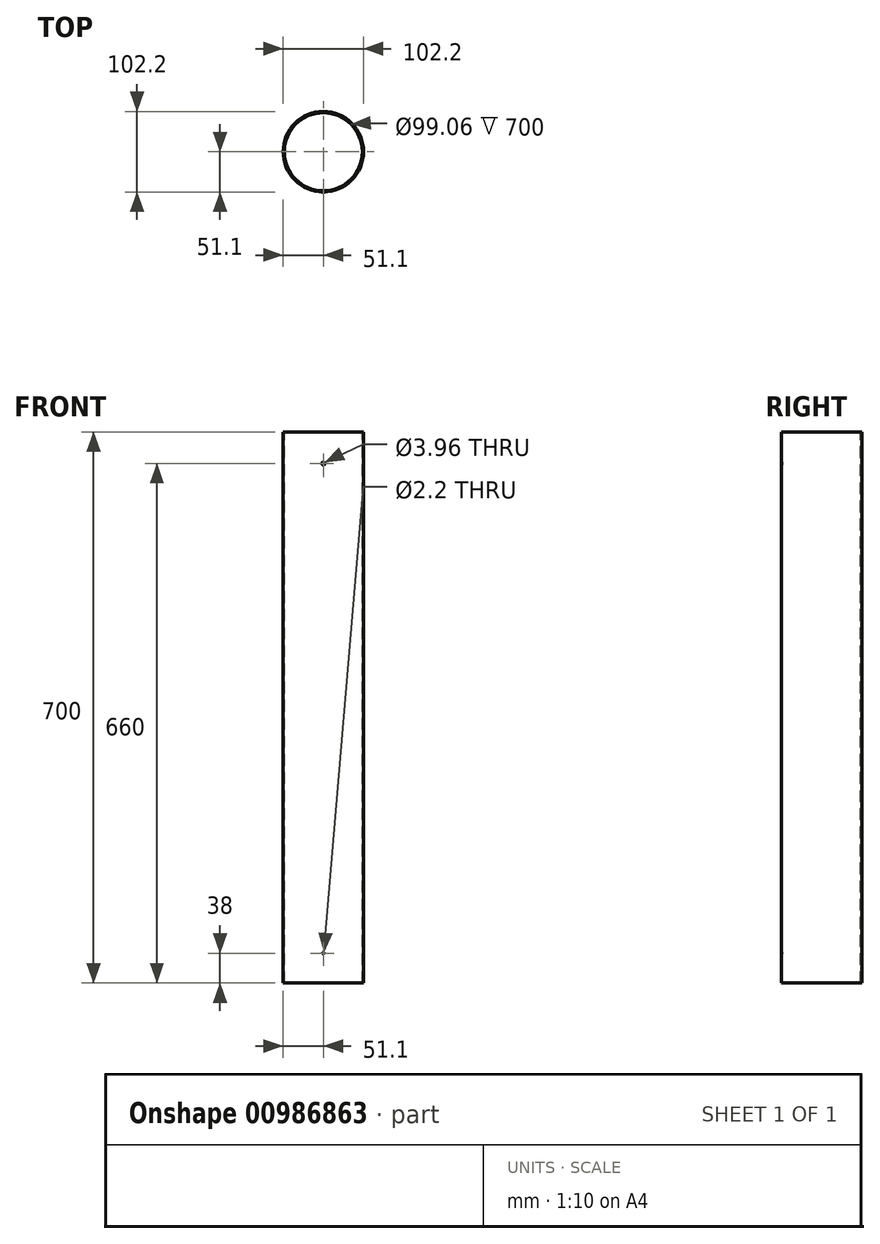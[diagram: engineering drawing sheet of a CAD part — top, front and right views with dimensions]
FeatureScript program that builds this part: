
annotation { "Feature Type Name" : "Feature", "Feature Type Description" : "" }
export const myFeature = defineFeature(function(context is Context, id is Id, definition is map)
    precondition{}
    {
        {
            var Q0;
            Q0=qCreatedBy(makeId("Front.planeOp"),FACE);
            var sketch = newSketch(context, id + "F0", { "sketchPlane" : qUnion([Q0])});
            skLineSegment(sketch, "E0", {"start": v(-51.1, 0) * mm, "end": v(-51.1, 700) * mm});
            skLineSegment(sketch, "E1", {"start": v(-51.1, 700) * mm, "end": v(-49.53, 700) * mm});
            skLineSegment(sketch, "E2", {"start": v(-49.53, 700) * mm, "end": v(-49.53, 0) * mm});
            skLineSegment(sketch, "E3", {"start": v(-49.53, 0) * mm, "end": v(-51.1, 0) * mm});
            skLineSegment(sketch, "E4", {"start": v(0, 0) * mm, "end": v(0, -97.37) * mm});
            skSolve(sketch);
        }
        {
            var Q0;
            Q0=qSketchRegion(id+"F0",true);
            var Q1;
            Q1=sQuery(id+"F0.wireOp",EDGE,"E4");
            revolve(context, id + "F1", {"surfaceOperationType" : NewSurfaceOperationType.NEW, "entities" : qUnion([Q0]), "axis" : qUnion([Q1]), "revolveType" : RevolveType.FULL});
        }
        {
            var Q0;
            Q0=qCreatedBy(makeId("Front.planeOp"),FACE);
            var sketch = newSketch(context, id + "F2", { "sketchPlane" : qUnion([Q0])});
            skCircle(sketch, "E5", {"center": v(0, 660) * mm, "radius": 1.98 * mm});
            skSolve(sketch);
        }
        {
            var Q0;
            Q0=qSketchRegion(id+"F2",true);
            extrude(context, id + "F3", {"entities" : qUnion([Q0]), "operationType" : NewBodyOperationType.REMOVE, "depth" : 60 * mm, "offsetDistance" : 25 * mm});
        }
        {
            var Q0;
            Q0=qCreatedBy(makeId("Front.planeOp"),FACE);
            var sketch = newSketch(context, id + "F4", { "sketchPlane" : qUnion([Q0])});
            skPoint(sketch, "E6", {"position": v(0, 38) * mm});
            skSolve(sketch);
        }
        {
            var Q0;
            Q0=sQuery(id+"F4.wireOp",VERTEX,"E6");
            var Q1;
            Q1=makeQuery(id+"F1.opRevolve","SWEPT_BODY",BODY,{"disambiguationData":[OSD([sQuery(id+"F0.wireOp",EDGE,"E0"),sQuery(id+"F0.wireOp",EDGE,"E1"),sQuery(id+"F0.wireOp",EDGE,"E2"),sQuery(id+"F0.wireOp",EDGE,"E3")])]});
            hole(context, id + "F5", {"style" : HoleStyle.SIMPLE, "endStyle" : HoleEndStyle.THROUGH, "oppositeDirection" : true, "holeDiameter" : 2.2 * mm, "majorDiameter" : 5 * mm, "isTappedThrough" : true, "tappedDepth" : 12 * mm, "tapClearance" : 3, "startFromSketch" : true, "locations" : qUnion([Q0]), "scope" : qUnion([Q1])});
        }
    });
